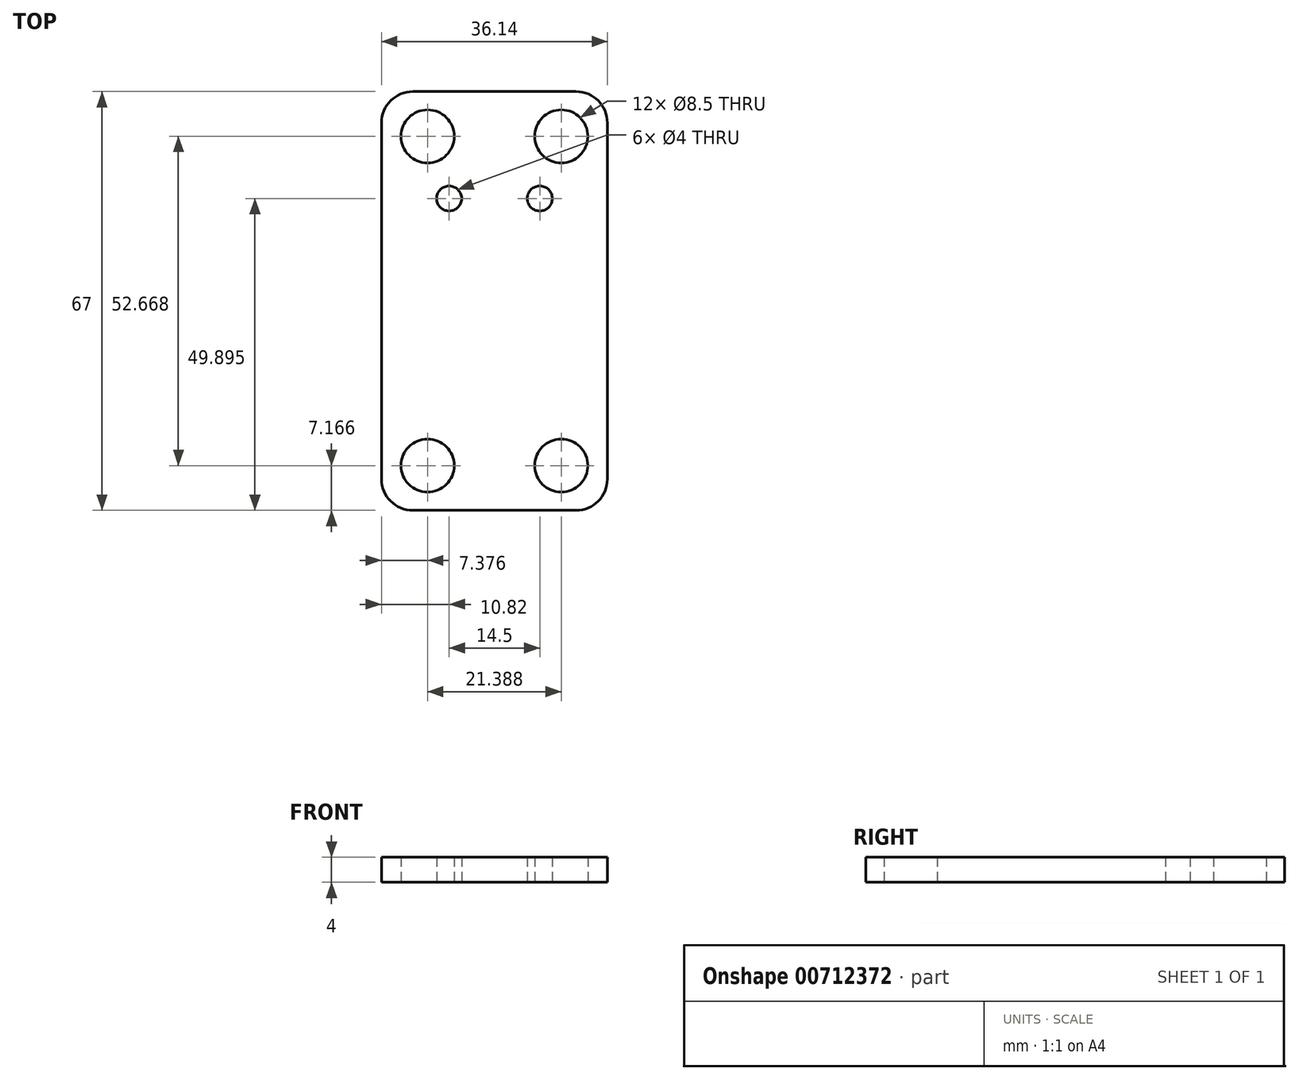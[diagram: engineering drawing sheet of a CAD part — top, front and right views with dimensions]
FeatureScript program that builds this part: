
annotation { "Feature Type Name" : "Feature", "Feature Type Description" : "" }
export const myFeature = defineFeature(function(context is Context, id is Id, definition is map)
    precondition{}
    {
        {
            var Q0;
            Q0=qCreatedBy(makeId("Top.planeOp"),FACE);
            var sketch = newSketch(context, id + "F0", { "sketchPlane" : qUnion([Q0])});
            skLineSegment(sketch, "E0.bottom", {"start": v(18.07, -33.5) * mm, "end": v(-18.06, -33.5) * mm});
            skLineSegment(sketch, "E0.top", {"start": v(18.07, 33.5) * mm, "end": v(-18.06, 33.5) * mm});
            skLineSegment(sketch, "E0.left", {"start": v(18.07, -33.5) * mm, "end": v(18.07, 33.5) * mm});
            skLineSegment(sketch, "E0.right", {"start": v(-18.06, -33.5) * mm, "end": v(-18.06, 33.5) * mm});
            skPoint(sketch, "E0.middle", {"position": v(0, 0) * mm});
            skLineSegment(sketch, "E1", {"start": v(-26.6, 30.66) * mm, "end": v(32.25, 30.66) * mm, "construction": true});
            skLineSegment(sketch, "E2", {"start": v(-14.96, 52.84) * mm, "end": v(-14.95, -51.77) * mm, "construction": true});
            skCircle(sketch, "E3", {"center": v(-10.7, 26.33) * mm, "radius": 4.25 * mm});
            skCircle(sketch, "E4.MirrorC", {"center": v(10.7, 26.33) * mm, "radius": 4.25 * mm});
            skCircle(sketch, "E5.MirrorC", {"center": v(-10.7, -26.33) * mm, "radius": 4.25 * mm});
            skCircle(sketch, "E6.MirrorC", {"center": v(10.7, -26.33) * mm, "radius": 4.25 * mm});
            skLineSegment(sketch, "E7", {"start": v(0, 16.4) * mm, "end": v(-7.25, 16.4) * mm, "construction": true});
            skCircle(sketch, "E8", {"center": v(-7.25, 16.4) * mm, "radius": 2 * mm});
            skCircle(sketch, "E9.MirrorC", {"center": v(7.25, 16.4) * mm, "radius": 2 * mm});
            skSolve(sketch);
        }
        {
            var Q0;
            Q0=makeQuery(id+"F0.imprint","IMPRINT",FACE,{"disambiguationData":[TD([[makeQuery(id+"F0.imprint","IMPRINT",EDGE,{"derivedFrom":sQuery(id+"F0.wireOp",EDGE,"E0.bottom")}),-1.0]])]});
            extrude(context, id + "F1", {"entities" : qUnion([Q0]), "depth" : 4 * mm, "offsetDistance" : 25 * mm});
        }
        {
            var Q0;
            Q0=makeQuery(id+"F1.opExtrude","SWEPT_EDGE",EDGE,{"disambiguationData":[OSD([sQuery(id+"F0.wireOp",EDGE,"E0.bottom"),sQuery(id+"F0.wireOp",EDGE,"E0.left")])]});
            var Q1;
            Q1=makeQuery(id+"F1.opExtrude","SWEPT_EDGE",EDGE,{"disambiguationData":[OSD([sQuery(id+"F0.wireOp",EDGE,"E0.bottom"),sQuery(id+"F0.wireOp",EDGE,"E0.right")])]});
            var Q2;
            Q2=makeQuery(id+"F1.opExtrude","SWEPT_EDGE",EDGE,{"disambiguationData":[OSD([sQuery(id+"F0.wireOp",EDGE,"E0.top"),sQuery(id+"F0.wireOp",EDGE,"E0.left")])]});
            var Q3;
            Q3=makeQuery(id+"F1.opExtrude","SWEPT_EDGE",EDGE,{"disambiguationData":[OSD([sQuery(id+"F0.wireOp",EDGE,"E0.top"),sQuery(id+"F0.wireOp",EDGE,"E0.right")])]});
            fillet(context, id + "F2", {"entities" : qUnion([Q0, Q1, Q2, Q3]), "radius" : 5 * mm, "tangentPropagation" : true, "allowEdgeOverflow" : false});
        }
    });
